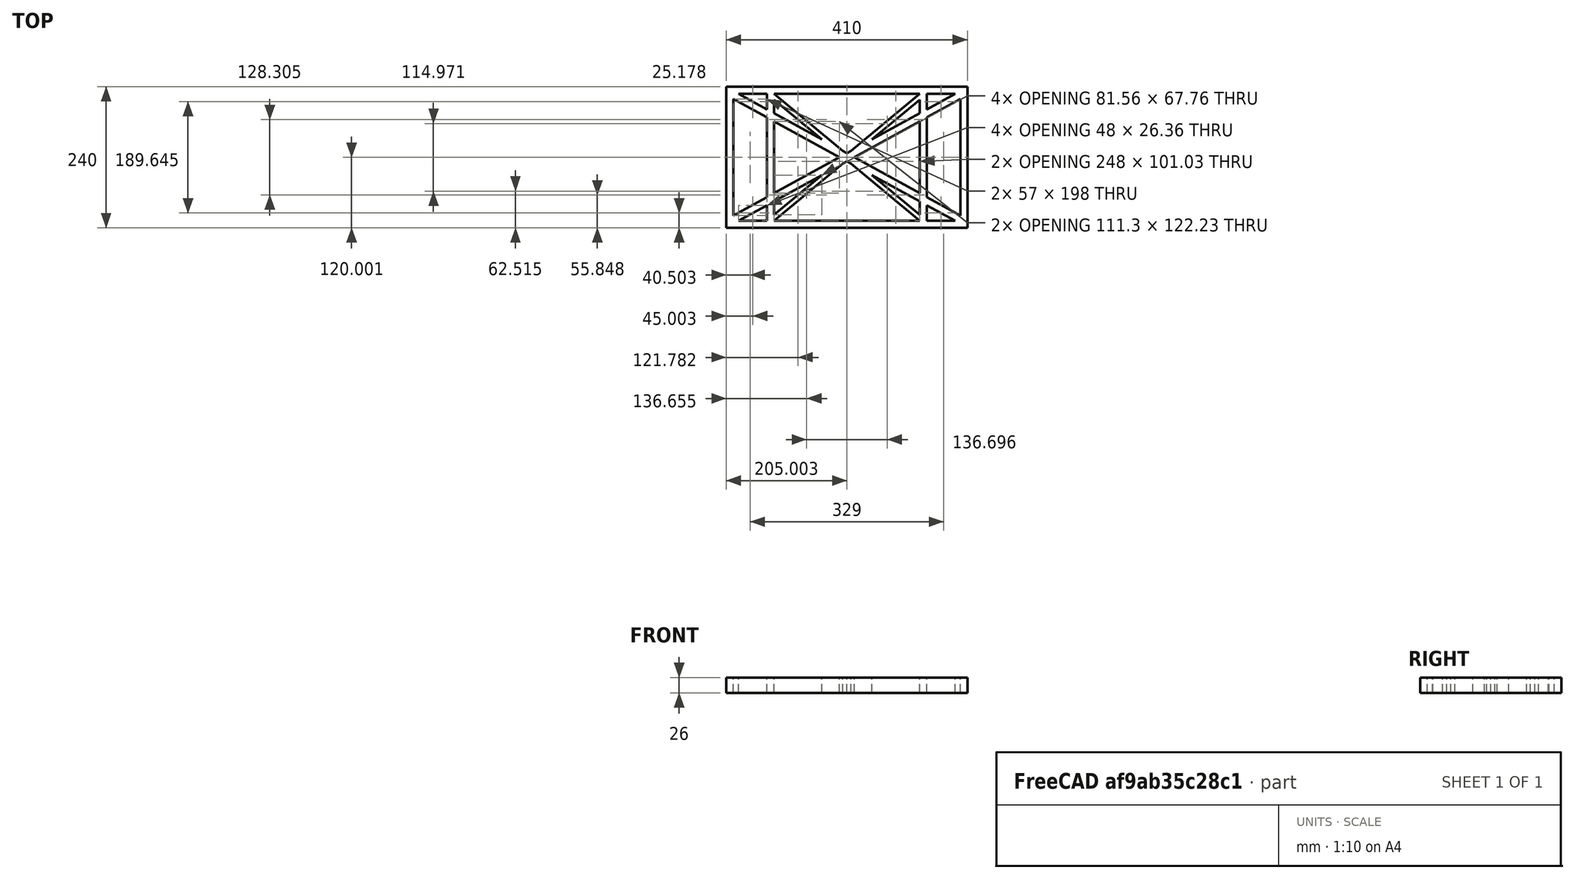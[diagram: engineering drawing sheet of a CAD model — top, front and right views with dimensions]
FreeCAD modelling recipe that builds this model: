
FCSTD DOCUMENT  (FreeCAD 0.19R0.19.2)
Label: laptopStand019
License: All rights reserved
LicenseURL: http://en.wikipedia.org/wiki/All_rights_reserved
objects: Sketcher::SketchObject×3, Part::Extrusion×1
note: 4 computed .brp shape members not serialized (recipe doc carries the construction recipe); baked Part::Feature solids carry a one-line shape summary decoded from their .brp

FEATURE [Sketcher::SketchObject] Sketch
  FullyConstrained = true
  sketch-geometry (52):
    g0: LineSegment StartX=-22.9272 StartY=136.221 StartZ=0 EndX=-22.9272 EndY=-103.779 EndZ=0
    g1: LineSegment StartX=-22.9272 StartY=136.221 StartZ=0 EndX=387.073 EndY=136.221 EndZ=0
    g2: LineSegment StartX=-22.9272 StartY=-103.779 StartZ=0 EndX=387.073 EndY=-103.779 EndZ=0
    g3: LineSegment StartX=387.073 StartY=136.221 StartZ=0 EndX=387.073 EndY=-103.779 EndZ=0
    g4: LineSegment StartX=375.073 StartY=115.221 StartZ=0 EndX=318.073 EndY=83.9235 EndZ=0
    g5: LineSegment StartX=-10.9272 StartY=-82.7794 StartZ=0 EndX=46.0728 EndY=-51.4823 EndZ=0
    g6: LineSegment StartX=-1.92719 StartY=124.221 StartZ=0 EndX=46.0728 EndY=97.8651 EndZ=0
    g7: LineSegment StartX=366.073 StartY=-91.7794 StartZ=0 EndX=318.073 EndY=-65.424 EndZ=0
    g8: LineSegment StartX=-10.9272 StartY=115.221 StartZ=0 EndX=-10.9272 EndY=-82.7794 EndZ=0
    g9: LineSegment StartX=375.073 StartY=-82.7794 StartZ=0 EndX=375.073 EndY=115.221 EndZ=0
    g10: LineSegment StartX=-1.92719 StartY=-91.7794 StartZ=0 EndX=46.0728 EndY=-91.7794 EndZ=0
    g11: LineSegment StartX=318.073 StartY=124.221 StartZ=0 EndX=366.073 EndY=124.221 EndZ=0
    g12: LineSegment StartX=306.073 StartY=-81.8102 StartZ=0 EndX=224.513 EndY=-14.0532 EndZ=0
    g13: LineSegment StartX=58.0728 StartY=114.251 StartZ=0 EndX=139.632 EndY=46.4944 EndZ=0
    g14: LineSegment StartX=306.073 StartY=124.221 StartZ=0 EndX=189.124 EndY=27.0628 EndZ=0
    g15: LineSegment StartX=58.0728 StartY=-91.7794 StartZ=0 EndX=175.022 EndY=5.37834 EndZ=0
    g16: LineSegment StartX=46.0728 StartY=124.221 StartZ=0 EndX=46.0728 EndY=97.8651 EndZ=0
    g17: LineSegment StartX=58.0728 StartY=-81.8102 StartZ=0 EndX=58.0728 EndY=-58.8351 EndZ=0
    g18: LineSegment StartX=318.073 StartY=124.221 StartZ=0 EndX=318.073 EndY=97.8651 EndZ=0
    g19: LineSegment StartX=306.073 StartY=114.251 StartZ=0 EndX=306.073 EndY=91.2763 EndZ=0
    g20: LineSegment StartX=182.073 StartY=23.1914 StartZ=0 EndX=189.124 EndY=27.0628 EndZ=0
    g21: LineSegment StartX=182.073 StartY=9.24976 StartZ=0 EndX=175.022 EndY=5.37834 EndZ=0
    g22: LineSegment StartX=224.513 StartY=46.4944 StartZ=0 EndX=306.073 EndY=114.251 EndZ=0
    g23: LineSegment StartX=175.022 StartY=27.0628 StartZ=0 EndX=58.0728 EndY=124.221 EndZ=0
    g24: LineSegment StartX=169.377 StartY=16.2206 StartZ=0 EndX=58.0728 EndY=77.3346 EndZ=0
    g25: LineSegment StartX=139.632 StartY=-14.0532 StartZ=0 EndX=58.0728 EndY=-81.8102 EndZ=0
    g26: LineSegment StartX=194.768 StartY=16.2206 StartZ=0 EndX=306.073 EndY=-44.8935 EndZ=0
    g27: LineSegment StartX=224.513 StartY=46.4944 StartZ=0 EndX=306.073 EndY=91.2763 EndZ=0
    g28: LineSegment StartX=175.022 StartY=27.0628 StartZ=0 EndX=182.073 EndY=23.1914 EndZ=0
    g29: LineSegment StartX=139.632 StartY=-14.0532 StartZ=0 EndX=58.0728 EndY=-58.8351 EndZ=0
    g30: LineSegment StartX=189.124 StartY=5.37834 StartZ=0 EndX=182.073 EndY=9.24976 EndZ=0
    g31: LineSegment StartX=189.124 StartY=5.37834 StartZ=0 EndX=306.073 EndY=-91.7794 EndZ=0
    g32: LineSegment StartX=306.073 StartY=77.3346 StartZ=0 EndX=306.073 EndY=-44.8935 EndZ=0
    g33: LineSegment StartX=318.073 StartY=83.9235 StartZ=0 EndX=318.073 EndY=-51.4823 EndZ=0
    g34: LineSegment StartX=318.073 StartY=97.8651 StartZ=0 EndX=366.073 EndY=124.221 EndZ=0
    g35: LineSegment StartX=306.073 StartY=77.3346 StartZ=0 EndX=194.768 EndY=16.2206 EndZ=0
    g36: LineSegment StartX=306.073 StartY=-58.8351 StartZ=0 EndX=224.513 EndY=-14.0532 EndZ=0
    g37: LineSegment StartX=306.073 StartY=-58.8351 StartZ=0 EndX=306.073 EndY=-81.8102 EndZ=0
    g38: LineSegment StartX=318.073 StartY=-51.4823 StartZ=0 EndX=375.073 EndY=-82.7794 EndZ=0
    g39: LineSegment StartX=318.073 StartY=-65.424 StartZ=0 EndX=318.073 EndY=-91.7794 EndZ=0
    g40: LineSegment StartX=306.073 StartY=124.221 StartZ=0 EndX=58.0728 EndY=124.221 EndZ=0
    g41: LineSegment StartX=318.073 StartY=-91.7794 StartZ=0 EndX=366.073 EndY=-91.7794 EndZ=0
    g42: LineSegment StartX=58.0728 StartY=-91.7794 StartZ=0 EndX=306.073 EndY=-91.7794 EndZ=0
    g43: LineSegment StartX=58.0728 StartY=-44.8935 StartZ=0 EndX=58.0728 EndY=77.3346 EndZ=0
    g44: LineSegment StartX=46.0728 StartY=-65.424 StartZ=0 EndX=-1.92719 EndY=-91.7794 EndZ=0
    g45: LineSegment StartX=46.0728 StartY=-65.424 StartZ=0 EndX=46.0728 EndY=-91.7794 EndZ=0
    g46: LineSegment StartX=58.0728 StartY=-44.8935 StartZ=0 EndX=169.377 EndY=16.2206 EndZ=0
    g47: LineSegment StartX=58.0728 StartY=91.2763 StartZ=0 EndX=58.0728 EndY=114.251 EndZ=0
    g48: LineSegment StartX=46.0728 StartY=83.9235 StartZ=0 EndX=46.0728 EndY=-51.4823 EndZ=0
    g49: LineSegment StartX=46.0728 StartY=124.221 StartZ=0 EndX=-1.92719 EndY=124.221 EndZ=0
    g50: LineSegment StartX=58.0728 StartY=91.2763 StartZ=0 EndX=139.632 EndY=46.4944 EndZ=0
    g51: LineSegment StartX=46.0728 StartY=83.9235 StartZ=0 EndX=-10.9272 EndY=115.221 EndZ=0
  constraints (102):
    c: Vertical(g0)
    c: Distance(g0) = 240
    c: Horizontal(g1)
    c: Distance(g1) = 410
    c: Coincident(g1,g0)
    c: Coincident(g2,g0)
    c: Horizontal(g2)
    c: Coincident(g3,g1)
    c: Vertical(g3)
    c: Coincident(g2,g3)
    c: Block(g1)
    c: Horizontal(g10)
    c: Horizontal(g11)
    c: PointOnObject(g35,g6)
    c: Coincident(g28,g20)
    c: Coincident(g30,g21)
    c: Tangent(g7,g24)
    c: PointOnObject(g24,g5)
    c: PointOnObject(g26,g4)
    c: Coincident(g20,g14)
    c: Tangent(g20,g27)
    c: Coincident(g50,g13)
    c: Coincident(g28,g23)
    c: Coincident(g22,g27)
    c: Coincident(g21,g15)
    c: Coincident(g29,g25)
    c: Tangent(g21,g29)
    c: Coincident(g36,g12)
    c: Coincident(g31,g30)
    c: Coincident(g22,g19)
    c: Tangent(g19,g32)
    c: Tangent(g18,g33)
    c: Coincident(g27,g19)
    c: Tangent(g27,g34)
    c: Coincident(g4,g33)
    c: Coincident(g35,g32)
    c: Tangent(g4,g35)
    c: Coincident(g37,g12)
    c: Tangent(g7,g36)
    c: Tangent(g32,g37)
    c: Coincident(g26,g32)
    c: Tangent(g26,g38)
    c: Coincident(g33,g38)
    c: Coincident(g39,g7)
    c: Tangent(g33,g39)
    c: Coincident(g25,g17)
    c: Tangent(g17,g43)
    c: Coincident(g29,g17)
    c: Tangent(g29,g44)
    c: Coincident(g45,g44)
    c: Tangent(g16,g45)
    c: Coincident(g5,g48)
    c: Coincident(g46,g43)
    c: Tangent(g5,g46)
    c: Tangent(g43,g47)
    c: Tangent(g16,g48)
    c: Coincident(g13,g47)
    c: PointOnObject(g40,g23)
    c: Tangent(g40,g49)
    c: Coincident(g6,g16)
    c: Coincident(g50,g47)
    c: Tangent(g6,g50)
    c: Coincident(g24,g43)
    c: Coincident(g51,g48)
    c: Tangent(g24,g51)
    c: Block(g23)
    c: Block(g14)
    c: Block(g20)
    c: Block(g40)
    c: Block(g18)
    c: Block(g34)
    c: Block(g4)
    c: Block(g38)
    c: Block(g9)
    c: Block(g36)
    c: Block(g37)
    c: Block(g7)
    c: Block(g39)
    c: Block(g22)
    c: Block(g31)
    c: Block(g42)
    c: Block(g21)
    c: Block(g15)
    c: Block(g29)
    c: Block(g25)
    c: Block(g45)
    c: Block(g44)
    c: Block(g5)
    c: Block(g8)
    c: Block(g51)
    c: Block(g6)
    c: Block(g16)
    c: Block(g13)
    c: Block(g47)
    c: Block(g35)
    c: Block(g32)
    c: Block(g24)
    c: Block(g46)
    c: Block(g49)
    c: Block(g11)
    c: Block(g41)
    c: Block(g10)
FEATURE [Part::Extrusion] Extrude
  Base = -> Sketch
  Dir = (0,0,1)
  DirMode = 2
  FaceMakerClass = Part::FaceMakerBullseye
  LengthFwd = 26
  LengthRev = 0
  Solid = true
  Symmetric = false
FEATURE [Sketcher::SketchObject] Sketch001
  FullyConstrained = true
  MapMode = 4
  Placement = pos=(0,0,0) rot=(0.57735,0.57735,0.57735;2.0944rad)
  Support = -> [Sketch]
  sketch-geometry (8):
    g0: LineSegment StartX=17.2228 StartY=-16.0875 StartZ=0 EndX=117.223 EndY=-16.0875 EndZ=0
    g1: LineSegment StartX=17.2228 StartY=-16.0875 StartZ=0 EndX=17.2228 EndY=-19.0875 EndZ=0
    g2: LineSegment StartX=117.223 StartY=-16.0875 StartZ=0 EndX=117.223 EndY=-19.0875 EndZ=0
    g3: BSplineCurve PolesCount=3 KnotsCount=2 Degree=2 IsPeriodic=0
    g4: BSplineCurve PolesCount=4 KnotsCount=2 Degree=3 IsPeriodic=0
    g5: LineSegment StartX=94.6577 StartY=-26.1351 StartZ=0 EndX=24.2583 EndY=-213.335 EndZ=0
    g6: LineSegment StartX=-9.4377 StartY=-200.664 StartZ=0 EndX=24.2583 EndY=-213.335 EndZ=0
    g7: LineSegment StartX=-9.4377 StartY=-200.664 StartZ=0 EndX=56.3505 EndY=-25.7249 EndZ=0
  constraints (20):
    c: Horizontal(g0)
    c: Distance(g0) = 100
    c: Block(g0)
    c: Coincident(g1,g0)
    c: Vertical(g1)
    c: Distance(g1) = 3
    c: Coincident(g2,g0)
    c: Vertical(g2)
    c: Distance(g2) = 3
    c: Block(g3)
    c: Coincident(g3,g2)
    c: Block(g4)
    c: Coincident(g5,g3)
    c: Block(g5)
    c: Distance(g6) = 36
    c: Perpendicular(g6,g5)
    c: Coincident(g6,g5)
    c: Distance(g7) = 186.9
    c: Parallel(g5,g7)
    c: Coincident(g7,g6)
FEATURE [Sketcher::SketchObject] Sketch002
  FullyConstrained = true
  Placement = pos=(0,0,0) rot=(-1,0,0;4.71239rad)
